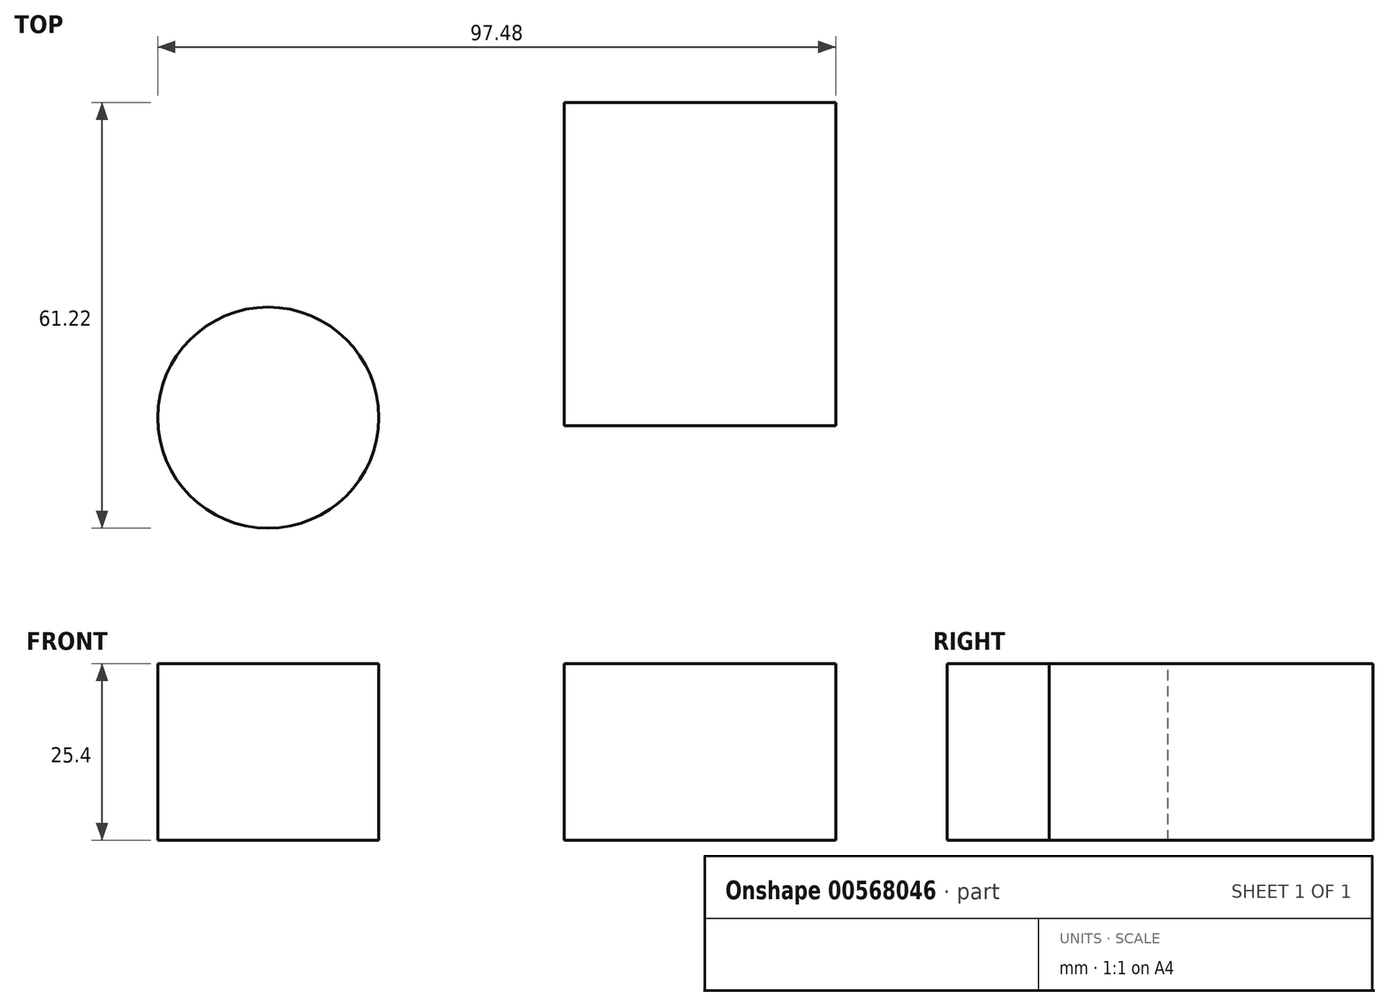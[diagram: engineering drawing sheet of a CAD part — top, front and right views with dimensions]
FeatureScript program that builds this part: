
annotation { "Feature Type Name" : "Feature", "Feature Type Description" : "" }
export const myFeature = defineFeature(function(context is Context, id is Id, definition is map)
    precondition{}
    {
        {
            var Q0;
            Q0=qCreatedBy(makeId("Top.planeOp"),FACE);
            var sketch = newSketch(context, id + "F0", { "sketchPlane" : qUnion([Q0])});
            skLineSegment(sketch, "E0", {"start": v(-52.42, 15.57) * mm, "end": v(-9.66, 32.91) * mm});
            skLineSegment(sketch, "E1.bottom", {"start": v(-9.26, 24.04) * mm, "end": v(29.76, 24.04) * mm});
            skLineSegment(sketch, "E1.top", {"start": v(-9.26, -22.47) * mm, "end": v(29.76, -22.47) * mm});
            skLineSegment(sketch, "E1.left", {"start": v(-9.26, 24.04) * mm, "end": v(-9.26, -22.47) * mm});
            skLineSegment(sketch, "E1.right", {"start": v(29.76, 24.04) * mm, "end": v(29.76, -22.47) * mm});
            skCircle(sketch, "E2", {"center": v(-51.83, -21.28) * mm, "radius": 15.9 * mm});
            skSolve(sketch);
        }
        {
            var Q0;
            Q0 = qSketchRegion(id + "F0", true);
            extrude(context, id + "F1", {"entities" : qUnion([Q0]), "oppositeDirection" : true, "depth" : 25.4 * mm, "offsetDistance" : 25.4 * mm});
        }
    });
